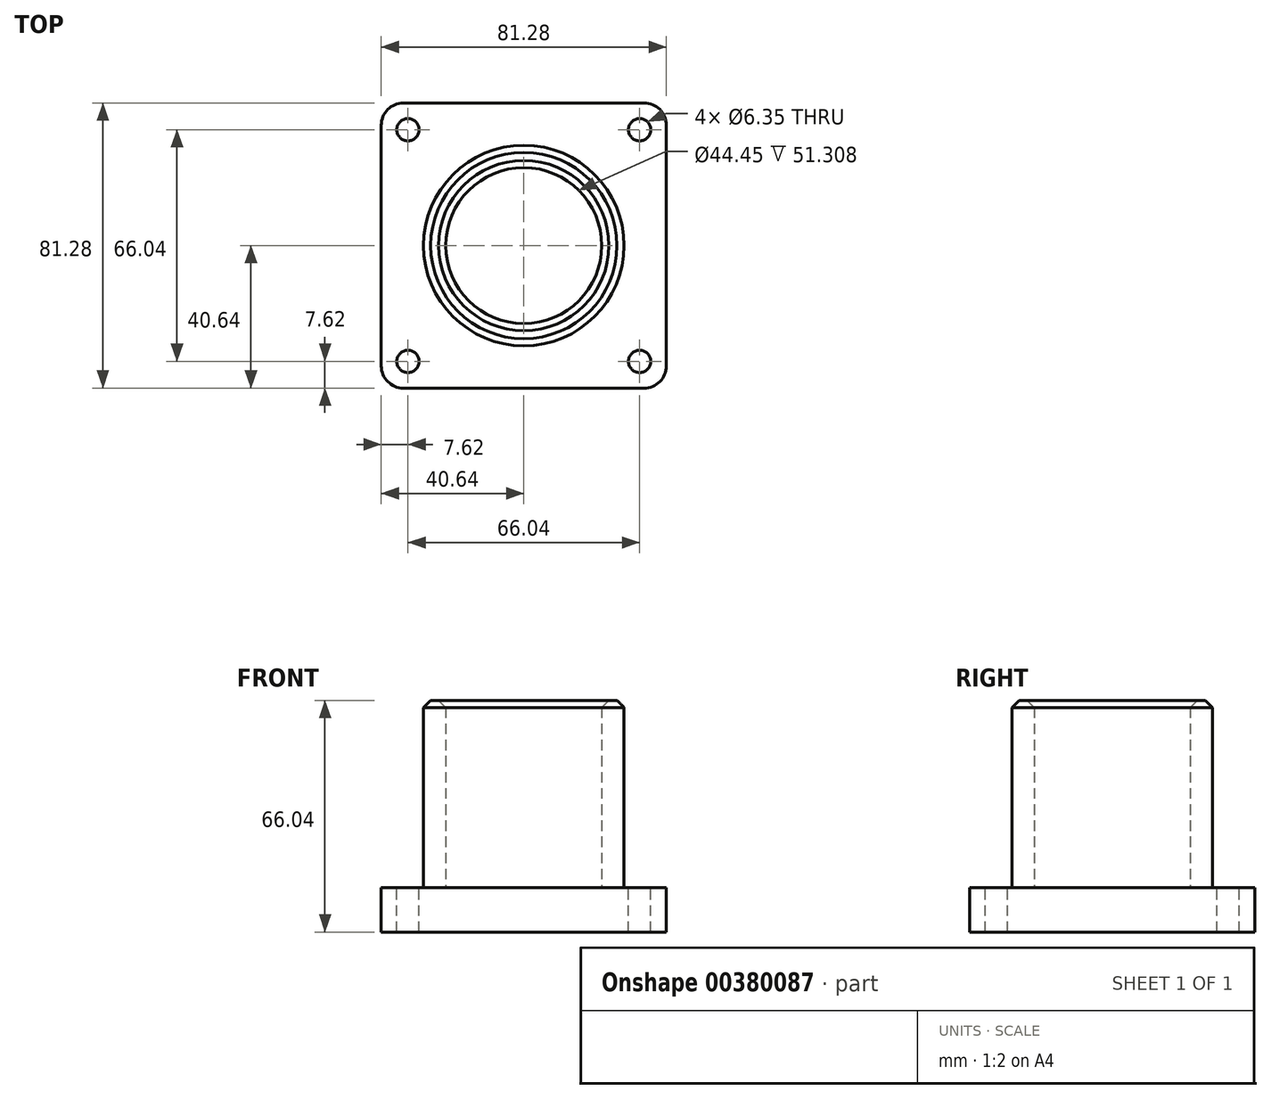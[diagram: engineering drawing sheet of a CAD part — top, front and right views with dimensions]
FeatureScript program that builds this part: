
annotation { "Feature Type Name" : "Feature", "Feature Type Description" : "" }
export const myFeature = defineFeature(function(context is Context, id is Id, definition is map)
    precondition{}
    {
        {
            var Q0;
            Q0=qCreatedBy(makeId("Top.planeOp"),FACE);
            var sketch = newSketch(context, id + "F0", { "sketchPlane" : qUnion([Q0])});
            skLineSegment(sketch, "E0.bottom", {"start": v(40.64, -40.64) * mm, "end": v(-40.64, -40.64) * mm});
            skLineSegment(sketch, "E0.top", {"start": v(40.64, 40.64) * mm, "end": v(-40.64, 40.64) * mm});
            skLineSegment(sketch, "E0.left", {"start": v(40.64, -40.64) * mm, "end": v(40.64, 40.64) * mm});
            skLineSegment(sketch, "E0.right", {"start": v(-40.64, -40.64) * mm, "end": v(-40.64, 40.64) * mm});
            skPoint(sketch, "E0.middle", {"position": v(0, 0) * mm});
            skSolve(sketch);
        }
        {
            var Q0;
            Q0=makeQuery(id+"F0.imprint","IMPRINT",FACE,{"disambiguationData":[TD([[makeQuery(id+"F0.imprint","IMPRINT",EDGE,{"derivedFrom":sQuery(id+"F0.wireOp",EDGE,"E0.bottom")}),-1.0]])]});
            extrude(context, id + "F1", {"entities" : qUnion([Q0]), "depth" : 12.7 * mm});
        }
        {
            var Q0;
            Q0=makeQuery(id+"F1.opExtrude","CAP_FACE",FACE,{"disambiguationData":[OSD([sQuery(id+"F0.wireOp",EDGE,"E0.bottom"),sQuery(id+"F0.wireOp",EDGE,"E0.top"),sQuery(id+"F0.wireOp",EDGE,"E0.left"),sQuery(id+"F0.wireOp",EDGE,"E0.right")])],"isStart":false});
            var sketch = newSketch(context, id + "F2", { "sketchPlane" : qUnion([Q0])});
            skCircle(sketch, "E1", {"center": v(0, 0) * mm, "radius": 28.58 * mm});
            skCircle(sketch, "E2", {"center": v(0, 0) * mm, "radius": 22.23 * mm});
            skSolve(sketch);
        }
        {
            var Q0;
            Q0=makeQuery(id+"F2.imprint","IMPRINT",FACE,{"disambiguationData":[TD([[makeQuery(id+"F2.imprint","IMPRINT",EDGE,{"derivedFrom":sQuery(id+"F2.wireOp",EDGE,"E1")}),1.0]])]});
            extrude(context, id + "F3", {"entities" : qUnion([Q0]), "operationType" : NewBodyOperationType.ADD, "depth" : 53.34 * mm});
        }
        {
            var Q0;
            {var subQ0=sQuery(id+"F0.wireOp",EDGE,"E0.left");var subQ1=sQuery(id+"F0.wireOp",EDGE,"E0.top");var subQ2=sQuery(id+"F0.wireOp",EDGE,"E0.right");var subQ3=sQuery(id+"F0.wireOp",EDGE,"E0.bottom");Q0=makeQuery(id+"F3.boolean.opBoolean","SPLIT",FACE,{"disambiguationData":[TD([makeQuery(id+"F1.opExtrude","SWEPT_FACE",FACE,{"disambiguationData":[OSD([subQ3])]})])],"derivedFrom":makeQuery(id+"F1.opExtrude","CAP_FACE",FACE,{"disambiguationData":[OSD([subQ3,subQ1,subQ0,subQ2])],"isStart":false})});}
            var sketch = newSketch(context, id + "F4", { "sketchPlane" : qUnion([Q0])});
            skCircle(sketch, "E3", {"center": v(33.02, 33.02) * mm, "radius": 3.18 * mm});
            skCircle(sketch, "E4", {"center": v(33.02, -33.02) * mm, "radius": 3.18 * mm});
            skCircle(sketch, "E5", {"center": v(-33.02, -33.02) * mm, "radius": 3.18 * mm});
            skCircle(sketch, "E6", {"center": v(-33.02, 33.02) * mm, "radius": 3.18 * mm});
            skSolve(sketch);
        }
        {
            var Q0;
            Q0=makeQuery(id+"F4.imprint","IMPRINT",FACE,{"disambiguationData":[TD([[makeQuery(id+"F4.imprint","IMPRINT",EDGE,{"derivedFrom":sQuery(id+"F4.wireOp",EDGE,"E3")}),1.0]])]});
            var Q1;
            Q1=makeQuery(id+"F4.imprint","IMPRINT",FACE,{"disambiguationData":[TD([[makeQuery(id+"F4.imprint","IMPRINT",EDGE,{"derivedFrom":sQuery(id+"F4.wireOp",EDGE,"E4")}),1.0]])]});
            var Q2;
            Q2=makeQuery(id+"F4.imprint","IMPRINT",FACE,{"disambiguationData":[TD([[makeQuery(id+"F4.imprint","IMPRINT",EDGE,{"derivedFrom":sQuery(id+"F4.wireOp",EDGE,"E5")}),1.0]])]});
            var Q3;
            Q3=makeQuery(id+"F4.imprint","IMPRINT",FACE,{"disambiguationData":[TD([[makeQuery(id+"F4.imprint","IMPRINT",EDGE,{"derivedFrom":sQuery(id+"F4.wireOp",EDGE,"E6")}),1.0]])]});
            extrude(context, id + "F5", {"entities" : qUnion([Q0, Q1, Q2, Q3]), "operationType" : NewBodyOperationType.REMOVE, "endBound" : BoundingType.THROUGH_ALL, "oppositeDirection" : true, "depth" : 25.4 * mm});
        }
        {
            var Q0;
            Q0=makeQuery(id+"F1.opExtrude","SWEPT_EDGE",EDGE,{"disambiguationData":[OSD([sQuery(id+"F0.wireOp",EDGE,"E0.bottom"),sQuery(id+"F0.wireOp",EDGE,"E0.right")])]});
            var Q1;
            Q1=makeQuery(id+"F1.opExtrude","SWEPT_EDGE",EDGE,{"disambiguationData":[OSD([sQuery(id+"F0.wireOp",EDGE,"E0.top"),sQuery(id+"F0.wireOp",EDGE,"E0.right")])]});
            var Q2;
            Q2=makeQuery(id+"F1.opExtrude","SWEPT_EDGE",EDGE,{"disambiguationData":[OSD([sQuery(id+"F0.wireOp",EDGE,"E0.top"),sQuery(id+"F0.wireOp",EDGE,"E0.left")])]});
            var Q3;
            Q3=makeQuery(id+"F1.opExtrude","SWEPT_EDGE",EDGE,{"disambiguationData":[OSD([sQuery(id+"F0.wireOp",EDGE,"E0.bottom"),sQuery(id+"F0.wireOp",EDGE,"E0.left")])]});
            fillet(context, id + "F6", {"entities" : qUnion([Q0, Q1, Q2, Q3]), "radius" : 6.35 * mm, "tangentPropagation" : true, "allowEdgeOverflow" : false});
        }
        {
            var Q0;
            Q0=makeQuery(id+"F3.opExtrude","CAP_EDGE",EDGE,{"disambiguationData":[OSD([sQuery(id+"F2.wireOp",EDGE,"E2")])],"isStart":false});
            var Q1;
            Q1=makeQuery(id+"F3.opExtrude","CAP_EDGE",EDGE,{"disambiguationData":[OSD([sQuery(id+"F2.wireOp",EDGE,"E1")])],"isStart":false});
            chamfer(context, id + "F7", {"entities" : qUnion([Q0, Q1]), "width" : 2.03 * mm, "tangentPropagation" : true});
        }
    });
